# Revit family: Table-Height_Adjustable-Teknion-BH_MT_Peninusla_Bevel_Post_Leg_Mid_Height-R2018
name_source: partatom
category: Furniture
revit_build: Autodesk Revit 2018 (Build: 20170223_1515(x64)
units: mm (PartAtom-declared; Revit-internal decimal feet)

## family parameters
Always vertical = Yes
Cut with Voids When Loaded = No
OmniClass Number = 23.40.20.00
OmniClass Title = General Furniture and Specialties
Room Calculation Point = No
Shared = Yes
Work Plane-Based = No

## types (4) — shared parameters
Assembly Code = E2020200
Manufacturer = Teknion
Manufacturer Fax = 416.661.4586
Part Number = BH_MT
Product Documentation Link = https://www.teknion.com
Product Line = Expansion Casegoods
Product Page URL = https://www.teknion.com
Series = Expansion Casegoods
Sustainability Data = https://www.teknion.com
URL = www.teknion.com
Unit Weight URL = http://www.teknion.com
Warranty = http://www.teknion.com

## per-type parameters (varying)
| type | Description | Has End of Worksurface - Rectangular & Square | Has No Grommet | Model | Square Grommet Cut-out Hole Depth | Worksurface Thickness |
| 1-9/16" Worksurface Thickness, Mid-Height Configuration, End of Worksurface - Rectangular & Square Grommet | Height-Adjustable Meeting Peninsula – Bevel Post Leg – Mid-Height, 1-9/16" Worksurface Thickness, Mid-Height Configuration, End of Worksurface - Rectangular & Square Grommet, Extended Range- 26" to 48" | Yes | No | BHXMTK____F_E_ | 6 " | 1.555 " |
| 1-3/16" Worksurface Thickness, Mid-Height Configuration, End of Worksurface - Rectangular & Square Grommet | Height-Adjustable Meeting Peninsula – Bevel Post Leg – Mid-Height, 1-3/16" Worksurface Thickness, Mid-Height Configuration, End of Worksurface - Rectangular & Square Grommet, Extended Range- 26" to 48" | Yes | No | BHMMTK____F_E_ | 6 " | 1.189 " |
| 1-3/16" Worksurface Thickness, Mid-Height Configuration, No Grommet | Height-Adjustable Meeting Peninsula – Bevel Post Leg – Mid-Height, 1-3/16" Worksurface Thickness, Mid-Height Configuration, No Grommet, Extended Range- 26" to 48" | No | Yes | BHMMTK____N_E_ | 0.5 " | 1.189 " |
| 1-9/16" Worksurface Thickness, Mid-Height Configuration, No Grommet | Height-Adjustable Meeting Peninsula – Bevel Post Leg – Mid-Height, 1-9/16" Worksurface Thickness, Mid-Height Configuration, No Grommet, Extended Range- 26" to 48" | No | Yes | BHXMTK____N_E_ | 0.5 " | 1.555 " |

## geometry (parser evidence)
native form markers: Sweep x3
no freeform markers — native parametric forms only
